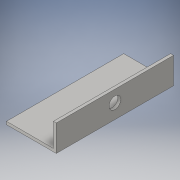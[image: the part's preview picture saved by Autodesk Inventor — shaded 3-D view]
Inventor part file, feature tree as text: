
AUTODESK INVENTOR PART (.ipt)
format: ipt  version: 2016 (Build 200138000, 138)  size: 105,984 bytes
history: native  units: in
note: dims shown in document units (in); Inventor stores cm internally (conversion verified against a paired STEP export)
features: extrude x3, sketch x3
ambient origin geometry x8: Origin, YZ Plane, XZ Plane, XY Plane, X Axis, Y Axis, Z Axis, Center Point
bodies: Solid1 (feature_tree)
feature tree (6):
  extrude  "Extrusion1"  Depth=5.0in
  extrude  "Extrusion2"  Depth=0.125in
  extrude  "Extrusion3"  Depth=0.125in
  sketch  "Sketch1"  dims[d0=2.125in d1=5.0in]
  sketch  "Sketch2"  dims[d2=0.125in d3=0.0in d4=0.125in]
  sketch  "Sketch3"  dims[d5=1.0in d6=0.0in d7=0.5in d8=0.5in d9=2.5in d10=0.125in d11=0.0in]
